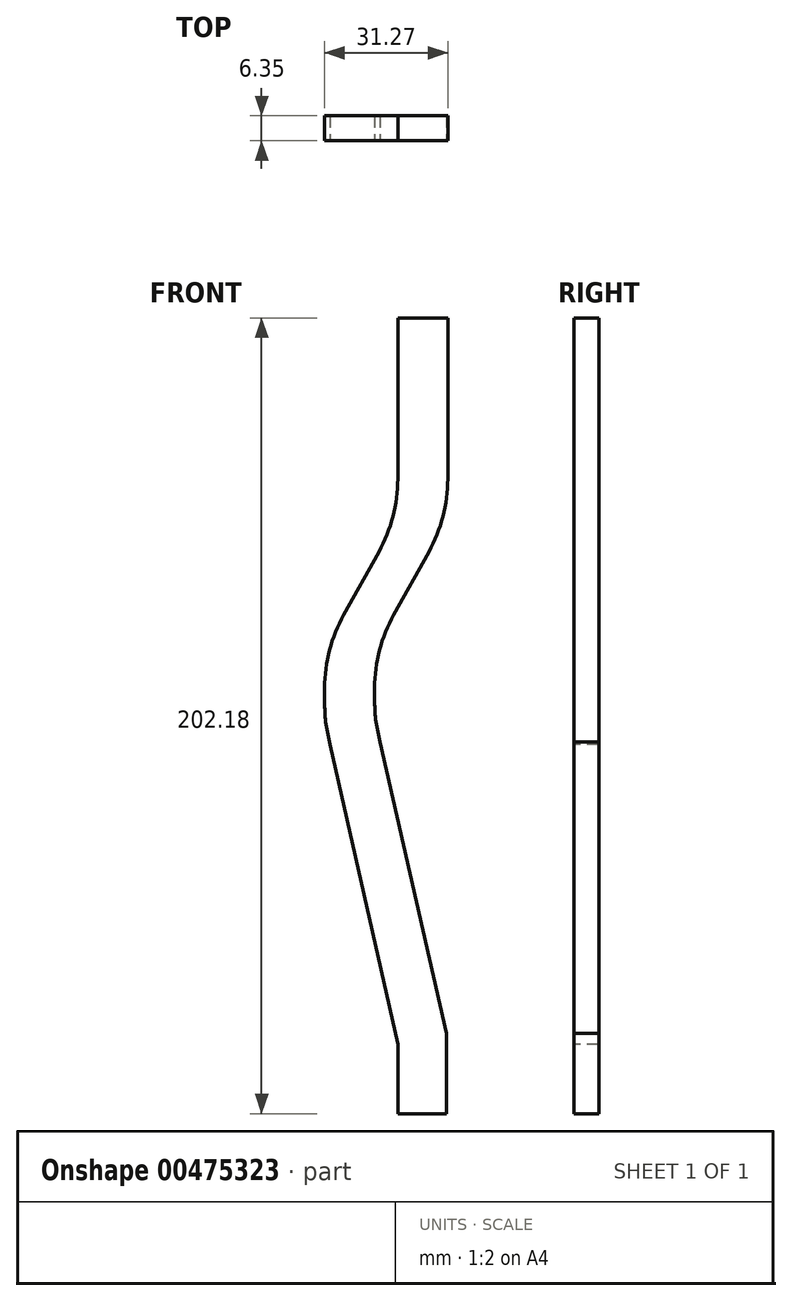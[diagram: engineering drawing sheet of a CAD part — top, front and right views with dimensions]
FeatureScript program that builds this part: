
annotation { "Feature Type Name" : "Feature", "Feature Type Description" : "" }
export const myFeature = defineFeature(function(context is Context, id is Id, definition is map)
    precondition{}
    {
        {
            var Q0;
            Q0=qCreatedBy(makeId("Front.planeOp"),FACE);
            var sketch = newSketch(context, id + "F0", { "sketchPlane" : qUnion([Q0])});
            skLineSegment(sketch, "E0", {"start": v(-18.57, 198.12) * mm, "end": v(-18.57, 202.27) * mm});
            skLineSegment(sketch, "E1", {"start": v(-13.74, 220.84) * mm, "end": v(-4.83, 236.8) * mm});
            skLineSegment(sketch, "E2", {"start": v(0, 255.36) * mm, "end": v(0, 296.25) * mm});
            skLineSegment(sketch, "E3", {"start": v(0, 296.25) * mm, "end": v(12.7, 296.25) * mm});
            skLineSegment(sketch, "E4", {"start": v(12.7, 296.25) * mm, "end": v(12.7, 255.36) * mm});
            skLineSegment(sketch, "E5", {"start": v(7.87, 236.8) * mm, "end": v(-1.04, 220.84) * mm});
            skLineSegment(sketch, "E6", {"start": v(-5.87, 202.27) * mm, "end": v(-5.87, 198.73) * mm});
            skPoint(sketch, "E7.visualSharp", {"position": v(-5.87, 212.18) * mm});
            skArc(sketch, "E7.filletArc", {"start": v(-1.04, 220.84) * mm, "mid": v(-4.64, 211.86) * mm, "end": v(-5.87, 202.27) * mm});
            skPoint(sketch, "E8.visualSharp", {"position": v(-5.87, 186.78) * mm});
            skArc(sketch, "E8.filletArc", {"start": v(-5.87, 198.73) * mm, "mid": v(-5.52, 193.58) * mm, "end": v(-4.48, 188.52) * mm});
            skPoint(sketch, "E9.visualSharp", {"position": v(-18.57, 212.18) * mm});
            skArc(sketch, "E9.filletArc", {"start": v(-13.74, 220.84) * mm, "mid": v(-17.34, 211.86) * mm, "end": v(-18.57, 202.27) * mm});
            skPoint(sketch, "E10.visualSharp", {"position": v(-18.57, 186.78) * mm});
            skArc(sketch, "E10.filletArc", {"start": v(-18.57, 198.12) * mm, "mid": v(-18.22, 192.93) * mm, "end": v(-17.16, 187.84) * mm});
            skPoint(sketch, "E11.visualSharp", {"position": v(12.7, 245.45) * mm});
            skArc(sketch, "E11.filletArc", {"start": v(7.87, 236.8) * mm, "mid": v(11.47, 245.77) * mm, "end": v(12.7, 255.36) * mm});
            skPoint(sketch, "E12.visualSharp", {"position": v(0, 245.45) * mm});
            skArc(sketch, "E12.filletArc", {"start": v(-4.83, 236.8) * mm, "mid": v(-1.23, 245.77) * mm, "end": v(0, 255.36) * mm});
            skPoint(sketch, "E13.visualSharp", {"position": v(0.16, 42.25) * mm});
            skLineSegment(sketch, "E14", {"start": v(-17.16, 187.84) * mm, "end": v(0, 111.64) * mm});
            skLineSegment(sketch, "E15", {"start": v(12.39, 114.43) * mm, "end": v(-4.48, 188.52) * mm});
            skLineSegment(sketch, "E16", {"start": v(0, 111.64) * mm, "end": v(0, 94.07) * mm});
            skLineSegment(sketch, "E17", {"start": v(0, 94.07) * mm, "end": v(12.39, 94.07) * mm});
            skLineSegment(sketch, "E18", {"start": v(12.39, 94.07) * mm, "end": v(12.39, 114.43) * mm});
            skSolve(sketch);
        }
        {
            var Q0;
            Q0=makeQuery(id+"F0.imprint","IMPRINT",FACE,{"disambiguationData":[TD([[makeQuery(id+"F0.imprint","IMPRINT",EDGE,{"derivedFrom":sQuery(id+"F0.wireOp",EDGE,"E0")}),-1.0]])]});
            extrude(context, id + "F1", {"entities" : qUnion([Q0]), "oppositeDirection" : true, "depth" : 6.35 * mm});
        }
    });
